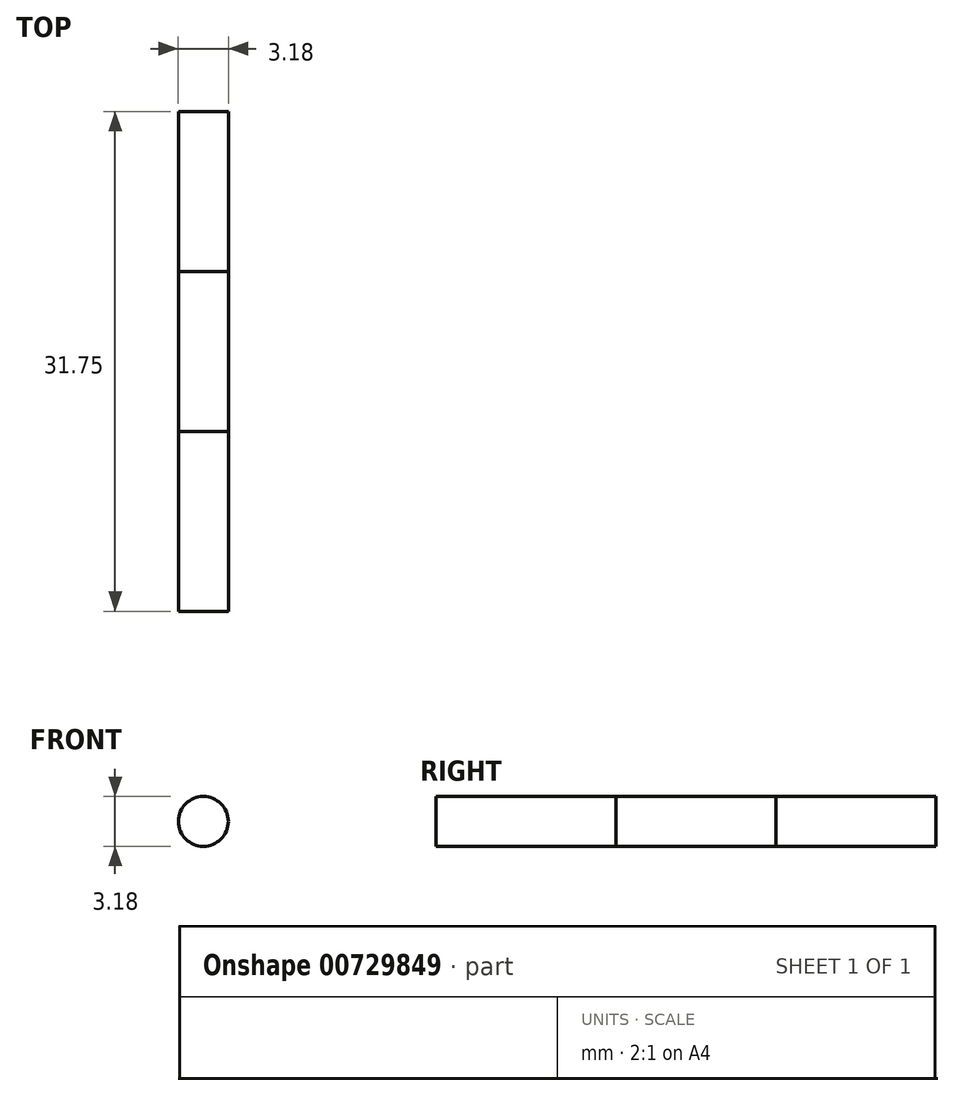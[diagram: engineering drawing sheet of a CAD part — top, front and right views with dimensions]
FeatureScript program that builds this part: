
annotation { "Feature Type Name" : "Feature", "Feature Type Description" : "" }
export const myFeature = defineFeature(function(context is Context, id is Id, definition is map)
    precondition{}
    {
        {
            var Q0;
            Q0=qCreatedBy(makeId("Front.planeOp"),FACE);
            var sketch = newSketch(context, id + "F0", { "sketchPlane" : qUnion([Q0])});
            skCircle(sketch, "E0", {"center": v(0, 0) * mm, "radius": 1.59 * mm});
            skSolve(sketch);
        }
        {
            var Q0;
            Q0 = qSketchRegion(id + "F0", true);
            extrude(context, id + "F1", {"entities" : qUnion([Q0]), "depth" : 10.16 * mm, "offsetDistance" : 25.4 * mm});
        }
        {
            var Q0;
            Q0=makeQuery(id+"F1.opExtrude","CAP_FACE",FACE,{"disambiguationData":[OSD([sQuery(id+"F0.wireOp",EDGE,"E0")])],"isStart":false});
            var sketch = newSketch(context, id + "F2", { "sketchPlane" : qUnion([Q0])});
            skCircle(sketch, "E1", {"center": v(0, 0) * mm, "radius": 1.59 * mm});
            skSolve(sketch);
        }
        {
            var Q0;
            Q0=makeQuery(id+"F2.imprint","IMPRINT",FACE,{"disambiguationData":[TD([[makeQuery(id+"F2.imprint","IMPRINT",EDGE,{"derivedFrom":sQuery(id+"F2.wireOp",EDGE,"E1")}),1.0]])]});
            extrude(context, id + "F3", {"entities" : qUnion([Q0]), "depth" : 10.16 * mm, "offsetDistance" : 25.4 * mm});
        }
        {
            var Q0;
            Q0=makeQuery(id+"F3.opExtrude","CAP_FACE",FACE,{"disambiguationData":[OSD([sQuery(id+"F2.wireOp",EDGE,"E1")])],"isStart":false});
            var sketch = newSketch(context, id + "F4", { "sketchPlane" : qUnion([Q0])});
            skCircle(sketch, "E2", {"center": v(0, 0) * mm, "radius": 1.59 * mm});
            skSolve(sketch);
        }
        {
            var Q0;
            Q0=makeQuery(id+"F4.imprint","IMPRINT",FACE,{"disambiguationData":[TD([[makeQuery(id+"F4.imprint","IMPRINT",EDGE,{"derivedFrom":sQuery(id+"F4.wireOp",EDGE,"E2")}),1.0]])]});
            extrude(context, id + "F5", {"entities" : qUnion([Q0]), "depth" : 11.43 * mm, "offsetDistance" : 25.4 * mm});
        }
    });
